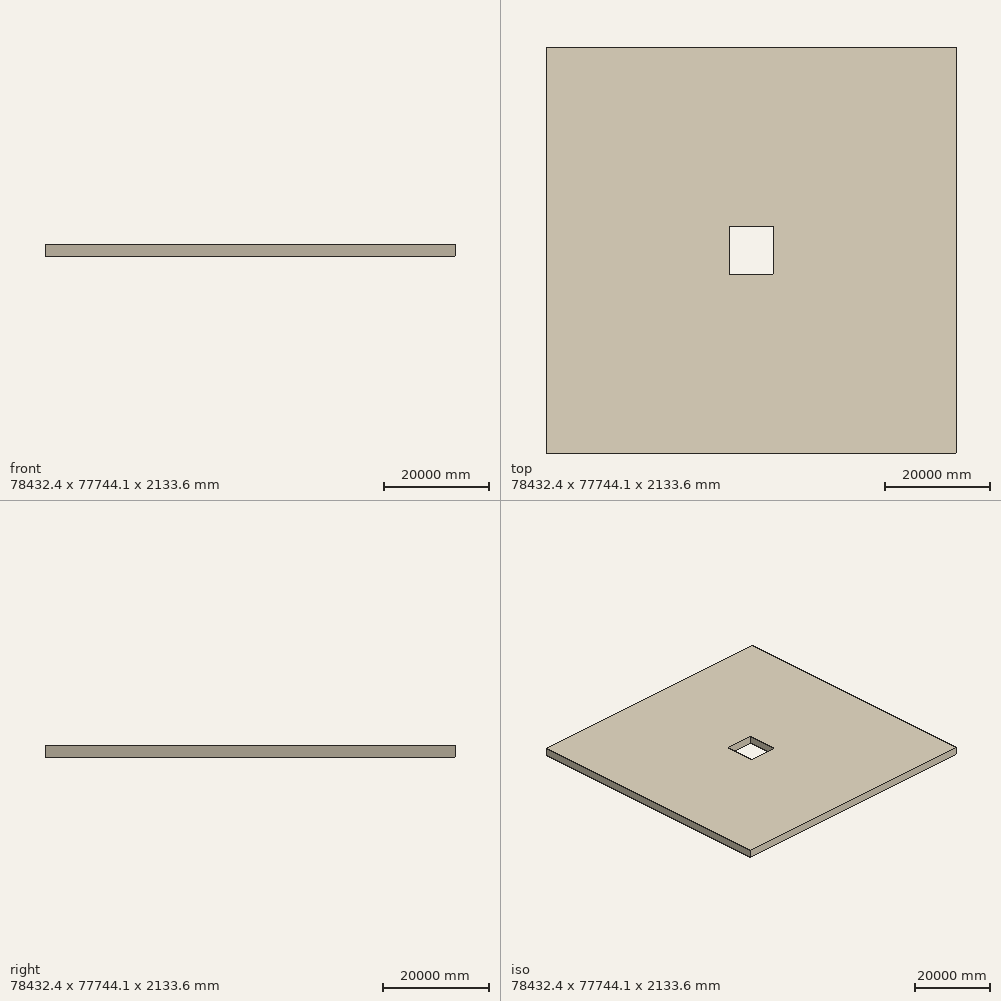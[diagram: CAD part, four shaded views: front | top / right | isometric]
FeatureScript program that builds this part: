
annotation { "Feature Type Name" : "Feature", "Feature Type Description" : "" }
export const myFeature = defineFeature(function(context is Context, id is Id, definition is map)
    precondition{}
    {
        {
            var Q0;
            Q0=qCreatedBy(makeId("Top.planeOp"),FACE);
            var sketch = newSketch(context, id + "F0", { "sketchPlane" : qUnion([Q0])});
            skLineSegment(sketch, "E0.bottom", {"start": v(4268.72, 4572) * mm, "end": v(-4268.72, 4572) * mm});
            skLineSegment(sketch, "E0.top", {"start": v(4268.72, -4572) * mm, "end": v(-4268.72, -4572) * mm});
            skLineSegment(sketch, "E0.left", {"start": v(4268.72, 4572) * mm, "end": v(4268.72, -4572) * mm});
            skLineSegment(sketch, "E0.right", {"start": v(-4268.72, 4572) * mm, "end": v(-4268.72, -4572) * mm});
            skPoint(sketch, "E0.middle", {"position": v(0, 0) * mm});
            skLineSegment(sketch, "E1.bottom", {"start": v(-39216.19, 38872.06) * mm, "end": v(39216.19, 38872.06) * mm});
            skLineSegment(sketch, "E1.top", {"start": v(-39216.19, -38872.06) * mm, "end": v(39216.19, -38872.06) * mm});
            skLineSegment(sketch, "E1.left", {"start": v(-39216.19, 38872.06) * mm, "end": v(-39216.19, -38872.06) * mm});
            skLineSegment(sketch, "E1.right", {"start": v(39216.19, 38872.06) * mm, "end": v(39216.19, -38872.06) * mm});
            skSolve(sketch);
        }
        {
            var Q0;
            Q0 = qSketchRegion(id + "F0", true);
            extrude(context, id + "F1", {"entities" : qUnion([Q0]), "oppositeDirection" : true, "depth" : 2133.6 * mm, "offsetDistance" : 30.48 * mm});
        }
    });
